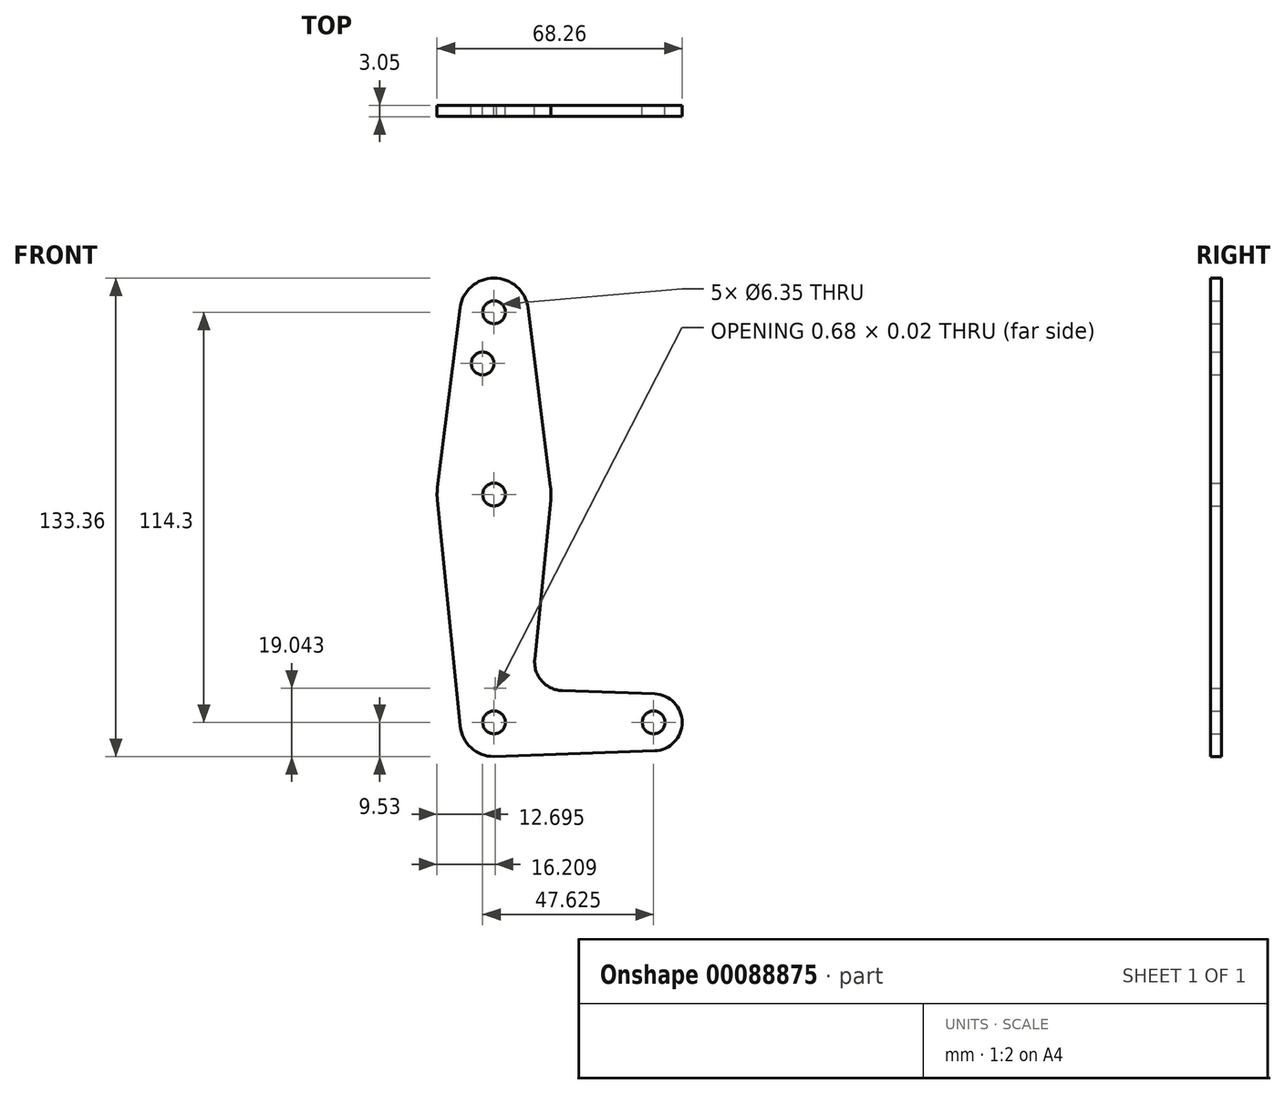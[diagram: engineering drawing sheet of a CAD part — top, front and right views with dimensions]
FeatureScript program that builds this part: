
annotation { "Feature Type Name" : "Feature", "Feature Type Description" : "" }
export const myFeature = defineFeature(function(context is Context, id is Id, definition is map)
    precondition{}
    {
        {
            var Q0;
            Q0=qCreatedBy(makeId("Front.planeOp"),FACE);
            var sketch = newSketch(context, id + "F0", { "sketchPlane" : qUnion([Q0])});
            skLineSegment(sketch, "E0", {"start": v(0, 0) * mm, "end": v(0, 114.3) * mm, "construction": true});
            skLineSegment(sketch, "E1", {"start": v(0, 0) * mm, "end": v(44.45, 0) * mm, "construction": true});
            skCircle(sketch, "E2", {"center": v(0, 0) * mm, "radius": 9.53 * mm});
            skCircle(sketch, "E3", {"center": v(44.45, 0) * mm, "radius": 7.94 * mm});
            skCircle(sketch, "E4", {"center": v(0, 63.5) * mm, "radius": 15.88 * mm});
            skCircle(sketch, "E5", {"center": v(0, 114.3) * mm, "radius": 9.53 * mm});
            skLineSegment(sketch, "E6", {"start": v(0, 9.52) * mm, "end": v(0, 9.52) * mm});
            skLineSegment(sketch, "E7", {"start": v(0, -9.52) * mm, "end": v(44.73, -7.93) * mm});
            skLineSegment(sketch, "E8", {"start": v(0, 63.5) * mm, "end": v(0, 0) * mm, "construction": true});
            skCircle(sketch, "E9", {"center": v(-3.18, 100.03) * mm, "radius": 3.18 * mm});
            skCircle(sketch, "E10", {"center": v(0, 114.3) * mm, "radius": 3.18 * mm});
            skCircle(sketch, "E11", {"center": v(0, 63.5) * mm, "radius": 3.18 * mm});
            skCircle(sketch, "E12", {"center": v(0, 0) * mm, "radius": 3.18 * mm});
            skCircle(sketch, "E13", {"center": v(44.45, 0) * mm, "radius": 3.18 * mm});
            skLineSegment(sketch, "E14", {"start": v(-3.18, 100.03) * mm, "end": v(0, 100.03) * mm});
            skLineSegment(sketch, "E15", {"start": v(-15.75, 65.48) * mm, "end": v(-9.45, 115.5) * mm});
            skLineSegment(sketch, "E16", {"start": v(15.75, 65.48) * mm, "end": v(9.45, 115.5) * mm});
            skLineSegment(sketch, "E17", {"start": v(-3.17, 100.03) * mm, "end": v(-3.17, 63.5) * mm, "construction": true});
            skLineSegment(sketch, "E18", {"start": v(0, 9.52) * mm, "end": v(0.68, 9.5) * mm});
            skLineSegment(sketch, "E19", {"start": v(18.97, 8.85) * mm, "end": v(44.73, 7.93) * mm});
            skLineSegment(sketch, "E20", {"start": v(15.8, 61.91) * mm, "end": v(11.34, 17.59) * mm});
            skPoint(sketch, "E21.visualSharp", {"position": v(10.5, 9.15) * mm});
            skArc(sketch, "E21.filletArc", {"start": v(11.34, 17.59) * mm, "mid": v(13.26, 11.57) * mm, "end": v(18.97, 8.85) * mm});
            skLineSegment(sketch, "E22", {"start": v(-15.8, 61.91) * mm, "end": v(-9.48, -0.95) * mm});
            skSolve(sketch);
        }
        {
            var Q0;
            {var subQ0=sQuery(id+"F0.wireOp",EDGE,"E7");var subQ1=sQuery(id+"F0.wireOp",EDGE,"E2");var subQ2=makeQuery(id+"F0.imprint","INTERSECT",VERTEX,{"disambiguationData":[OD(0.0)],"derivedFrom":[subQ1,subQ0]});Q0=makeQuery(id+"F0.imprint","IMPRINT",FACE,{"disambiguationData":[TD([[makeQuery(id+"F0.imprint","IMPRINT",EDGE,{"disambiguationData":[TD([[subQ2,-1.0]])],"derivedFrom":subQ1}),1.0]])]});}
            var Q1;
            Q1=makeQuery(id+"F0.imprint","IMPRINT",FACE,{"disambiguationData":[TD([[makeQuery(id+"F0.imprint","IMPRINT",EDGE,{"derivedFrom":sQuery(id+"F0.wireOp",EDGE,"E13")}),-1.0]])]});
            var Q2;
            Q2=makeQuery(id+"F0.imprint","IMPRINT",FACE,{"disambiguationData":[TD([[makeQuery(id+"F0.imprint","IMPRINT",EDGE,{"derivedFrom":sQuery(id+"F0.wireOp",EDGE,"E10")}),-1.0]])]});
            var Q3;
            Q3=makeQuery(id+"F0.imprint","IMPRINT",FACE,{"disambiguationData":[TD([[makeQuery(id+"F0.imprint","IMPRINT",EDGE,{"derivedFrom":sQuery(id+"F0.wireOp",EDGE,"E11")}),-1.0]])]});
            var Q4;
            Q4=makeQuery(id+"F0.imprint","IMPRINT",FACE,{"disambiguationData":[TD([[makeQuery(id+"F0.imprint","IMPRINT",EDGE,{"derivedFrom":sQuery(id+"F0.wireOp",EDGE,"E9")}),-1.0]])]});
            var Q5;
            Q5=makeQuery(id+"F0.imprint","IMPRINT",FACE,{"disambiguationData":[TD([[makeQuery(id+"F0.imprint","IMPRINT",EDGE,{"derivedFrom":sQuery(id+"F0.wireOp",EDGE,"E12")}),-1.0]])]});
            var Q6;
            {var subQ3=sQuery(id+"F0.wireOp",EDGE,"E19");Q6=makeQuery(id+"F0.imprint","IMPRINT",FACE,{"disambiguationData":[TD([[makeQuery(id+"F0.imprint","IMPRINT",EDGE,{"derivedFrom":subQ3}),-1.0]])]});}
            extrude(context, id + "F1", {"entities" : qUnion([Q0, Q1, Q2, Q3, Q4, Q5, Q6]), "depth" : 3.05 * mm});
        }
    });
